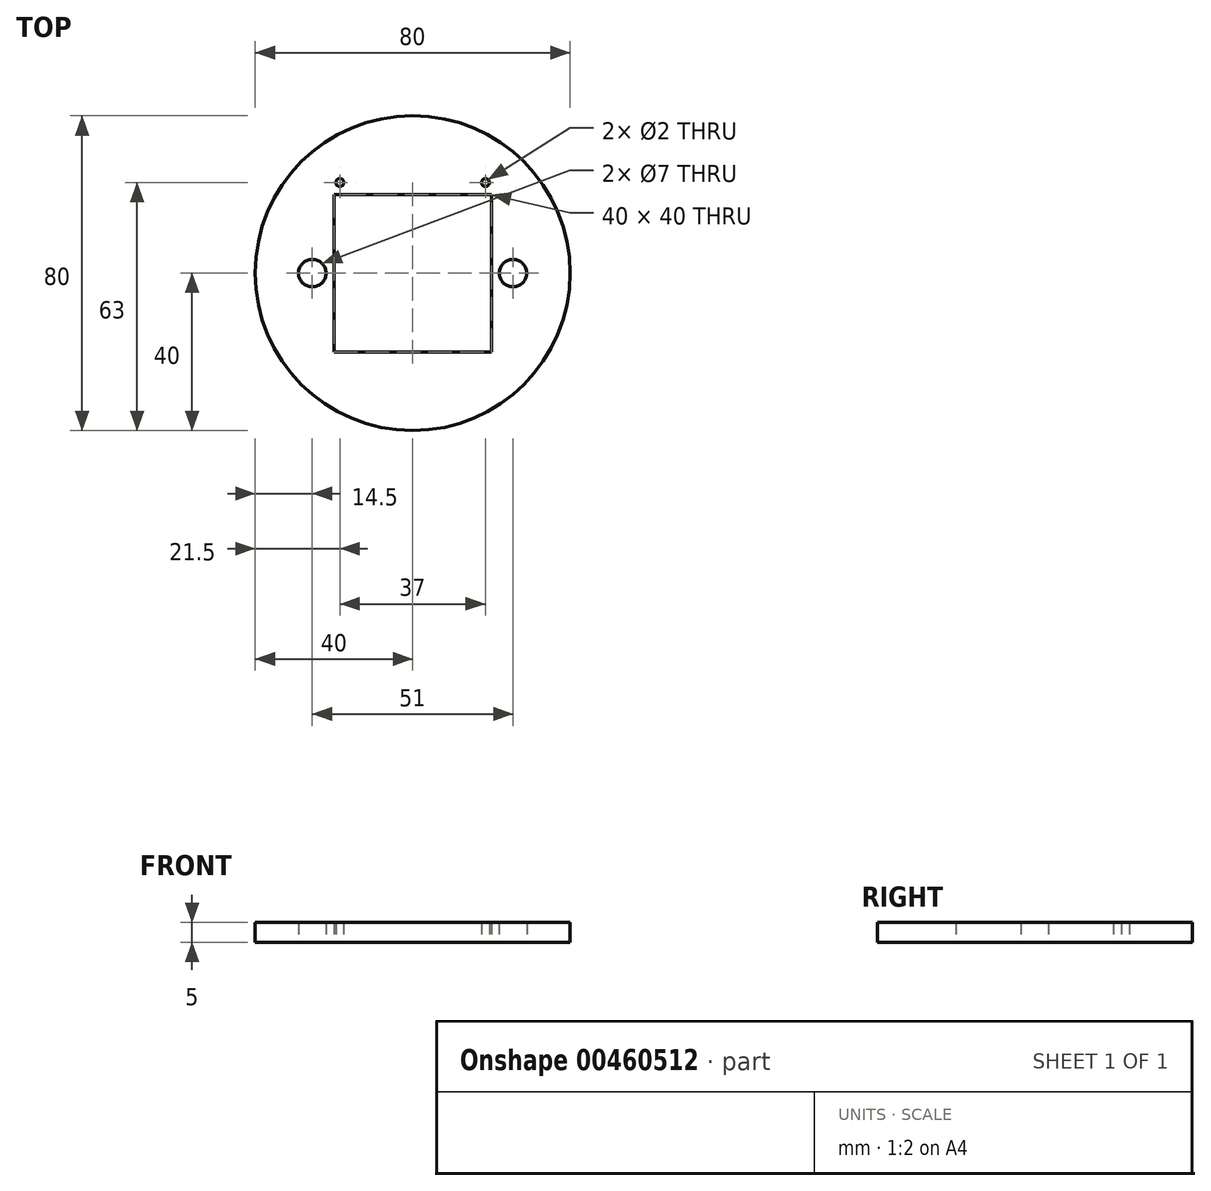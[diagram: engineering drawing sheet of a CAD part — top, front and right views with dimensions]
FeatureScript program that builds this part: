
annotation { "Feature Type Name" : "Feature", "Feature Type Description" : "" }
export const myFeature = defineFeature(function(context is Context, id is Id, definition is map)
    precondition{}
    {
        {
            var Q0;
            Q0=qCreatedBy(makeId("Top.planeOp"),FACE);
            var sketch = newSketch(context, id + "F0", { "sketchPlane" : qUnion([Q0])});
            skLineSegment(sketch, "E0.bottom", {"start": v(-20, 20) * mm, "end": v(20, 20) * mm});
            skLineSegment(sketch, "E0.top", {"start": v(-20, -20) * mm, "end": v(20, -20) * mm});
            skLineSegment(sketch, "E0.left", {"start": v(-20, 20) * mm, "end": v(-20, -20) * mm});
            skLineSegment(sketch, "E0.right", {"start": v(20, 20) * mm, "end": v(20, -20) * mm});
            skPoint(sketch, "E0.middle", {"position": v(0, 0) * mm});
            skCircle(sketch, "E1", {"center": v(25.5, 0) * mm, "radius": 3.5 * mm});
            skCircle(sketch, "E2", {"center": v(-25.5, 0) * mm, "radius": 3.5 * mm});
            skCircle(sketch, "E3", {"center": v(0, 0) * mm, "radius": 40 * mm});
            skCircle(sketch, "E4", {"center": v(-18.5, 23) * mm, "radius": 1 * mm});
            skPoint(sketch, "E5", {"position": v(-18.5, 20) * mm});
            skCircle(sketch, "E6", {"center": v(18.5, 23) * mm, "radius": 1 * mm});
            skPoint(sketch, "E7", {"position": v(18.5, 20) * mm});
            skPoint(sketch, "E8", {"position": v(0, 40) * mm});
            skPoint(sketch, "E9", {"position": v(0, -40) * mm});
            skPoint(sketch, "E10", {"position": v(-29, 0) * mm});
            skPoint(sketch, "E11", {"position": v(29, 0) * mm});
            skSolve(sketch);
        }
        {
            var Q0;
            Q0 = qSketchRegion(id + "F0", true);
            extrude(context, id + "F1", {"entities" : qUnion([Q0]), "depth" : 5 * mm});
        }
    });
